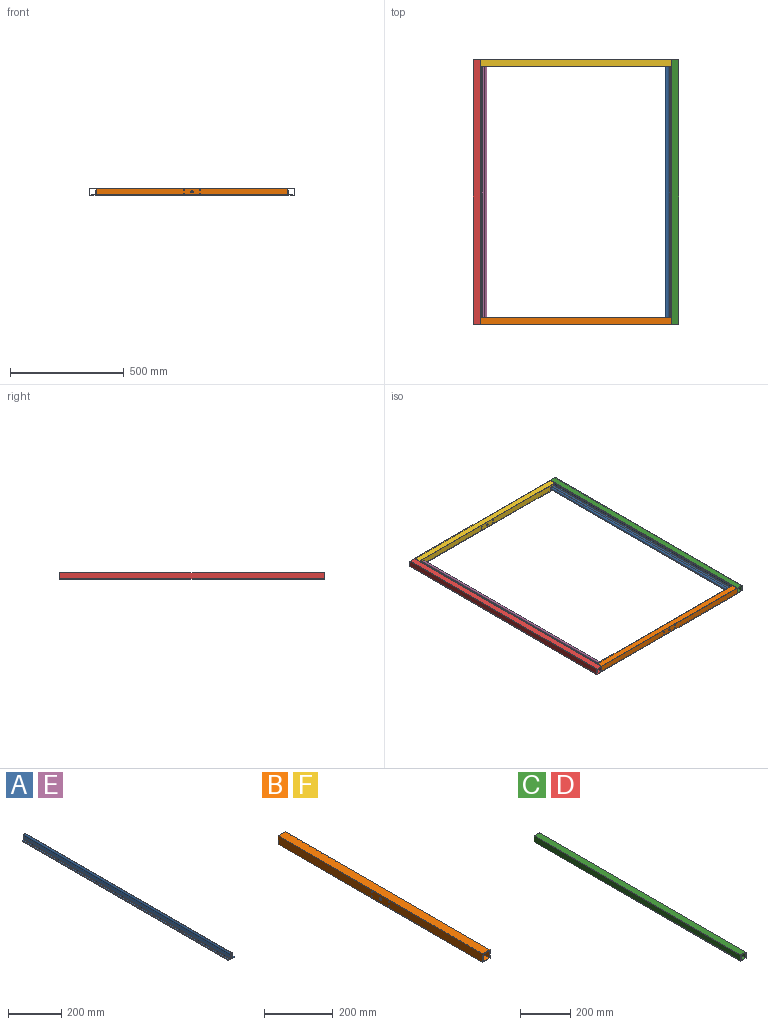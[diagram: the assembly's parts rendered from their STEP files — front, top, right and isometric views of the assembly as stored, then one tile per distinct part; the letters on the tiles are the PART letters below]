
ASSEMBLY  parts=6 mates=5
PART A: 50 faces, bbox 30x1100x29.5 mm
  f0: cylinder r=6.08mm len=1100mm, axis (0,-1,0), area 17950.8mm2, adj f1,f4,f6,f10,f23,f46
  f1: cylinder r=6.01mm len=1100mm, axis (0,-1,0), area 18450.8mm2, adj f0,f3,f5,f11,f23,f46
  f2: plane 1100x29.5mm, normal (0,0,-1), area 32233.8mm2, adj f3,f4,f5,f6,f7,f17,f18,f19
  f3: plane 29.44x13.75mm, normal (0,-1,0), area 161.1mm2, adj f1,f2,f11,f12,f13,f14,f15,f16
  f4: plane 29.25x13.25mm, normal (0,-1,0), area 143.9mm2, adj f0,f2,f7,f8,f9,f10,f46
  f5: plane 29.44x13.75mm, normal (0,1,0), area 161.1mm2, adj f1,f2,f11,f12,f13,f14,f15,f16
  f6: plane 29.25x13.25mm, normal (0,1,0), area 143.9mm2, adj f0,f2,f7,f8,f9,f10,f23
  f7: plane 1100x4.01mm, normal (1,0,0), area 4406.4mm2, adj f2,f4,f6,f8
  f8: plane 1100x8mm, normal (0,0,1), area 8697.8mm2, adj f4,f6,f7,f9,f19,f20,f21,f22
  f9: plane 1100x5.03mm, normal (1,0,0), area 5535.4mm2, adj f4,f6,f8,f10
  f10: plane 1100x8.94mm, normal (0.9,0,0.44), area 10924.8mm2, adj f0,f4,f6,f9
  f11: plane 1100x8.84mm, normal (-0.9,0,0.44), area 10798.6mm2, adj f1,f3,f5,f15
  f12: plane 1100x4.92mm, normal (-1,0,0), area 5409.2mm2, adj f3,f5,f13,f15
  f13: plane 1100x7.5mm, normal (0,0,1), area 8147.8mm2, adj f3,f5,f12,f16,f18,f24,f26,f27
  f14: plane 1100x3.01mm, normal (-1,0,0), area 3306.4mm2, adj f3,f5,f16,f17
  f15: cylinder r=0.5mm len=1100mm, axis (0,1,0), area 248.1mm2, adj f3,f5,f11,f12
  f16: cylinder r=0.5mm len=1100mm, axis (0,-1,0), area 863.9mm2, adj f3,f5,f13,f14
  f17: cylinder r=0.5mm len=1100mm, axis (0,1,0), area 863.9mm2, adj f2,f3,f5,f14
  f18: cylinder r=1.5mm len=4.01mm, axis (0,0,-1), area 37.8mm2, adj f2,f13
  f19: cylinder r=1.5mm len=4.01mm, axis (0,0,-1), area 37.8mm2, adj f2,f8
  f20: cylinder r=1.5mm len=4.01mm, axis (0,0,-1), area 37.8mm2, adj f2,f8
  f21: cylinder r=1.5mm len=4.01mm, axis (0,0,-1), area 37.8mm2, adj f2,f8
  f22: cylinder r=1.5mm len=4.01mm, axis (0,0,-1), area 37.8mm2, adj f2,f8
  f23: cylinder r=1.5mm len=29.52mm, axis (0,0,-1), area 138.7mm2, adj f0,f1,f2,f5,f6
  f24: cylinder r=1.5mm len=4.01mm, axis (0,0,-1), area 37.8mm2, adj f2,f13
  f25: cylinder r=1.5mm len=4.01mm, axis (0,0,-1), area 37.8mm2, adj f2,f8
  f26: cylinder r=1.5mm len=4.01mm, axis (0,0,-1), area 37.8mm2, adj f2,f13
  f27: cylinder r=1.5mm len=4.01mm, axis (0,0,-1), area 37.8mm2, adj f2,f13
  f28: cylinder r=1.5mm len=4.01mm, axis (0,0,-1), area 37.8mm2, adj f2,f8
  f29: cylinder r=1.5mm len=4.01mm, axis (0,0,-1), area 37.8mm2, adj f2,f13
  f30: cylinder r=1.5mm len=4.01mm, axis (0,0,-1), area 37.8mm2, adj f2,f13
  f31: cylinder r=1.5mm len=4.01mm, axis (0,0,-1), area 37.8mm2, adj f2,f8
  f32: cylinder r=1.5mm len=4.01mm, axis (0,0,-1), area 37.8mm2, adj f2,f8
  f33: cylinder r=1.5mm len=4.01mm, axis (0,0,-1), area 37.8mm2, adj f2,f8
  f34: cylinder r=1.5mm len=4.01mm, axis (0,0,-1), area 37.8mm2, adj f2,f13
  f35: cylinder r=1.5mm len=4.01mm, axis (0,0,-1), area 37.8mm2, adj f2,f13
  f36: cylinder r=1.5mm len=4.01mm, axis (0,0,-1), area 37.8mm2, adj f2,f13
  f37: cylinder r=1.5mm len=4.01mm, axis (0,0,-1), area 37.8mm2, adj f2,f13
  f38: cylinder r=1.5mm len=4.01mm, axis (0,0,-1), area 37.8mm2, adj f2,f8
  f39: cylinder r=1.5mm len=4.01mm, axis (0,0,-1), area 37.8mm2, adj f2,f13
  f40: cylinder r=1.5mm len=4.01mm, axis (0,0,-1), area 37.8mm2, adj f2,f8
  f41: cylinder r=1.5mm len=4.01mm, axis (0,0,-1), area 37.8mm2, adj f2,f13
  f42: cylinder r=1.5mm len=4.01mm, axis (0,0,-1), area 37.8mm2, adj f2,f13
  f43: cylinder r=1.5mm len=4.01mm, axis (0,0,-1), area 37.8mm2, adj f2,f8
  f44: cylinder r=1.5mm len=4.01mm, axis (0,0,-1), area 37.8mm2, adj f2,f13
  f45: cylinder r=1.5mm len=4.01mm, axis (0,0,-1), area 37.8mm2, adj f2,f8
  f46: cylinder r=1.5mm len=29.52mm, axis (0,0,-1), area 138.7mm2, adj f0,f1,f2,f3,f4
  f47: cylinder r=1.5mm len=4.01mm, axis (0,0,-1), area 37.8mm2, adj f2,f8
  f48: cylinder r=1.5mm len=4.01mm, axis (0,0,-1), area 37.8mm2, adj f2,f8
  f49: cylinder r=1.5mm len=4.01mm, axis (0,0,-1), area 37.8mm2, adj f2,f13
PART B: 20 faces, bbox 30x840x30 mm
  f0: plane 840x30mm, normal (1,0,0), area 25086.1mm2, adj f1,f7,f8,f9,f11,f13,f15,f17
  f1: plane 840x30mm, normal (0,0,1), area 25200mm2, adj f0,f2,f8,f9
  f2: plane 840x30mm, normal (-1,0,0), area 25086.1mm2, adj f1,f7,f8,f9,f10,f12,f14,f16
  f3: plane 840x26mm, normal (0,0,-1), area 21840mm2, adj f4,f6,f8,f9
  f4: plane 840x26mm, normal (-1,0,0), area 21726.1mm2, adj f3,f5,f8,f9,f11,f13,f15,f17
  f5: plane 840x26mm, normal (0,0,1), area 21840mm2, adj f4,f6,f8,f9
  f6: plane 840x26mm, normal (1,0,0), area 21726.1mm2, adj f3,f5,f8,f9,f10,f12,f14,f16
  f7: plane 840x30mm, normal (0,0,-1), area 25200mm2, adj f0,f2,f8,f9
  f8: plane 30x30mm, normal (0,-1,0), area 224mm2, adj f0,f1,f2,f3,f4,f5,f6,f7
  f9: plane 30x30mm, normal (0,1,0), area 224mm2, adj f0,f1,f2,f3,f4,f5,f6,f7
  f10: cylinder r=4.5mm len=9mm, axis (-1,0,0), area 56.5mm2, adj f2,f6
  f11: cylinder r=4.5mm len=9mm, axis (-1,0,0), area 56.5mm2, adj f0,f4
  f12: cylinder r=2mm len=4mm, axis (1,0,0), area 25.1mm2, adj f2,f6
  f13: cylinder r=2mm len=4mm, axis (1,0,0), area 25.1mm2, adj f0,f4
  f14: cylinder r=2mm len=4mm, axis (1,0,0), area 25.1mm2, adj f2,f6
  f15: cylinder r=2mm len=4mm, axis (1,0,0), area 25.1mm2, adj f0,f4
  f16: cylinder r=2mm len=4mm, axis (1,0,0), area 25.1mm2, adj f2,f6
  f17: cylinder r=2mm len=4mm, axis (1,0,0), area 25.1mm2, adj f0,f4
  f18: cylinder r=2mm len=4mm, axis (1,0,0), area 25.1mm2, adj f2,f6
  f19: cylinder r=2mm len=4mm, axis (1,0,0), area 25.1mm2, adj f0,f4
PART C: 10 faces, bbox 30x1160x30 mm
  f0: plane 1160x30mm, normal (1,0,0), area 34800mm2, adj f1,f7,f8,f9
  f1: plane 1160x30mm, normal (0,0,1), area 34800mm2, adj f0,f2,f8,f9
  f2: plane 1160x30mm, normal (-1,0,0), area 34800mm2, adj f1,f7,f8,f9
  f3: plane 1160x26mm, normal (0,0,-1), area 30160mm2, adj f4,f6,f8,f9
  f4: plane 1160x26mm, normal (-1,0,0), area 30160mm2, adj f3,f5,f8,f9
  f5: plane 1160x26mm, normal (0,0,1), area 30160mm2, adj f4,f6,f8,f9
  f6: plane 1160x26mm, normal (1,0,0), area 30160mm2, adj f3,f5,f8,f9
  f7: plane 1160x30mm, normal (0,0,-1), area 34800mm2, adj f0,f2,f8,f9
  f8: plane 30x30mm, normal (0,-1,0), area 224mm2, adj f0,f1,f2,f3,f4,f5,f6,f7
  f9: plane 30x30mm, normal (0,1,0), area 224mm2, adj f0,f1,f2,f3,f4,f5,f6,f7
PART D: same geometry as C
PART E: same geometry as A
PART F: same geometry as B
PLACE A rot(axis=(0,-1,0),90deg) t=(761.82,-282.43,-54.8)mm
PLACE B rot(axis=(0,0,-1),90deg) t=(341.82,-246.92,-39.3)mm
PLACE C t=(776.82,267.57,-39.3)mm
PLACE D t=(-93.18,267.57,-39.3)mm
PLACE E rot(axis=(0,1,0),90deg) t=(-78.18,-282.43,-24.3)mm
PLACE F rot(axis=(0,0,1),90deg) t=(341.82,782.06,-39.3)mm
MATE fastened B.f7 <-> D.f7  axis (0,0,1) through (-78.18,-312.43,-54.3)mm
MATE fastened C.f7 <-> B.f7  axis (0,0,1) through (761.82,-312.43,-54.3)mm
MATE fastened F.f7 <-> D.f7  axis (0,0,1) through (-78.18,847.57,-54.3)mm
MATE fastened A.f2 <-> C.f2  axis (1,0,0) through (761.82,267.57,-54.3)mm
MATE fastened E.f2 <-> D.f0  axis (-1,0,0) through (-78.18,267.57,-54.3)mm
